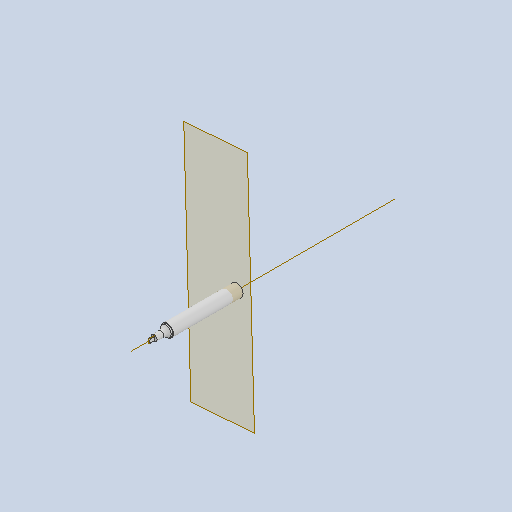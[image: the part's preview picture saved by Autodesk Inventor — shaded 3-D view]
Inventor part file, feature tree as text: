
AUTODESK INVENTOR PART (.ipt)
format: ipt  version: 2023.1 (Build 271208000, 208)  size: 161,792 bytes
history: native  units: mm
features: plane x2, sketch x2, revolve x1, other x1, extrude x1
ambient origin geometry x8: Origin, YZ Plane, XZ Plane, XY Plane, X Axis, Y Axis, Z Axis, Center Point
bodies: Solid1 (feature_tree)
feature tree (7):
  revolve  "Revolution1"  [1 undecoded]
  plane  "Work Plane1"
  other  "Work Axis2"
  plane  "Work Plane2"
  extrude  "Extrusion2"  Depth=2.0mm
  sketch  "Sketch1"  dims[d0=95.0mm d1=16.7mm]
  sketch  "Sketch3"  dims[d2=2.0mm d3=14.4mm d4=7.0mm d6=8.0mm d7=18.0mm d8=90.0deg d21=2.0mm d22=0.0mm]
note: 1 required parameter value undecoded (feature->parameter linkage not recoverable at this tier; creation-order binding heuristic only, values carry confidence <= 0.55)
